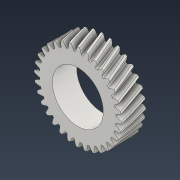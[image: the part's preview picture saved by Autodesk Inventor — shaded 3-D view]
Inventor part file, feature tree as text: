
AUTODESK INVENTOR PART (.ipt)
format: ipt  version: 2022 (Build 260153000, 153)  size: 542,720 bytes
history: native  units: mm (DEFAULTED — no unit token found)
features: plane x3, other x3, sketch x3, extrude x2
ambient origin geometry x8: Origin, YZ Plane, XZ Plane, XY Plane, X Axis, Y Axis, Z Axis, Center Point
bodies: Solid1 (feature_tree)
feature tree (11):
  extrude  "Extrusion1"  Depth=20.0mm TaperAngle=0.0deg
  plane  "Work Plane2"
  plane  "Work Plane8"
  plane  "Work Plane9"
  other  "Spur Gear"
  extrude  "Extrusion2"  Depth=10.0mm TaperAngle=0.0deg
  sketch  "Sketch1"  dims[d0=71.898447mm d1=20.0mm d2=0.0mm]
  sketch  "Sketch2"  dims[d3=68.107377mm d4=10.0mm d5=0.0mm]
  other  "Srf1"
  sketch  "Sketch3"  dims[d16=104.0mm d17=0.0mm d34=0.981748mm d39=0.0mm d41=0.0mm d43=104.0mm d46=104.0mm d47=0.0mm d48=0.0mm d49=42.0mm d50=0.0mm d51=0.0mm]
  other  "Pitch Diameter"
